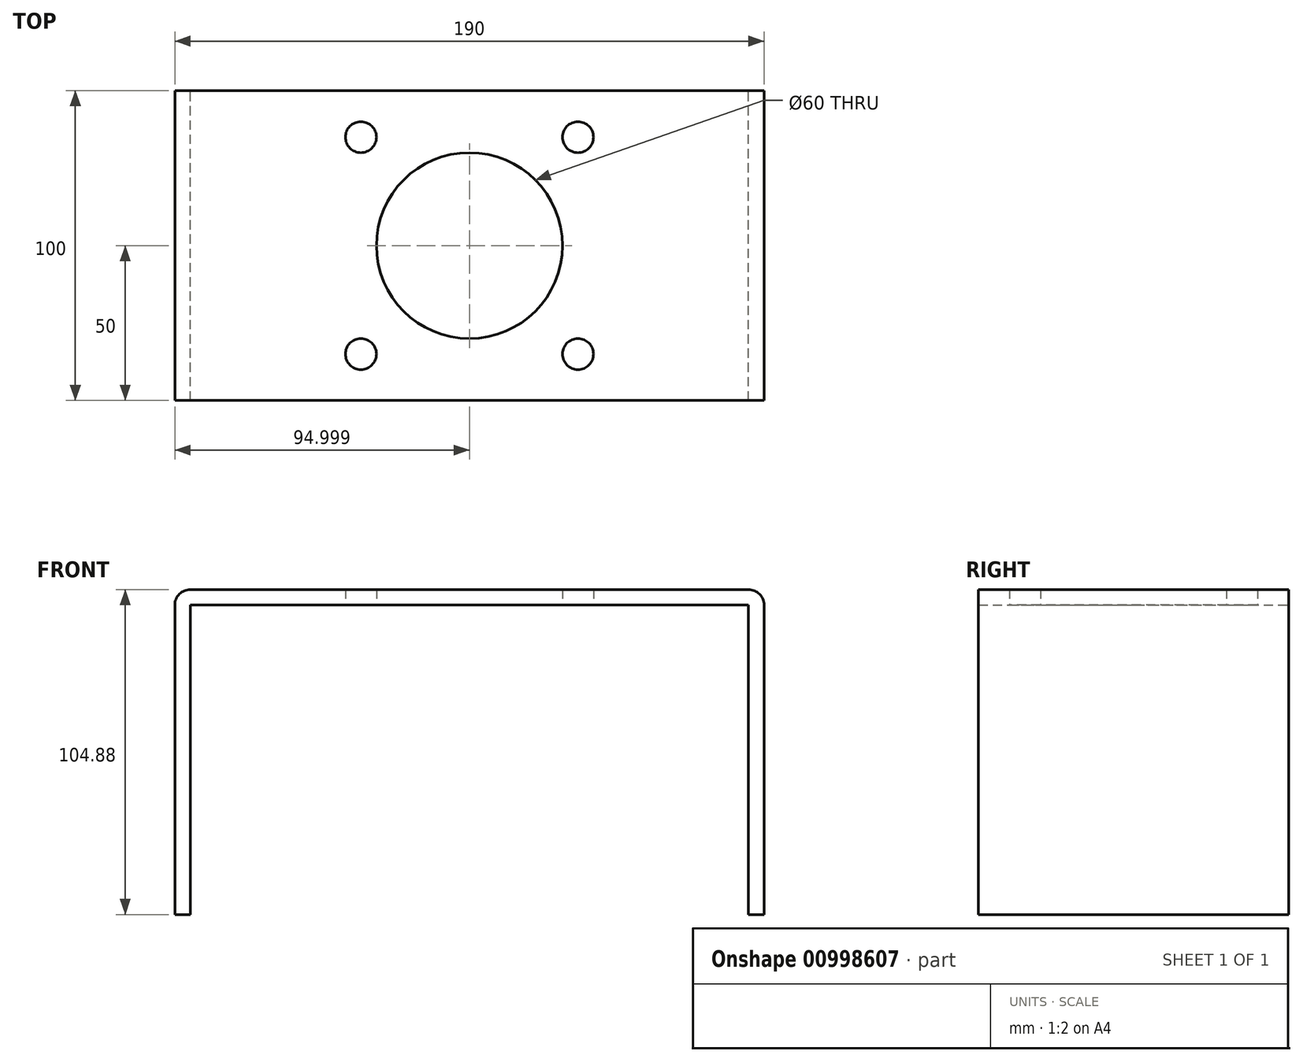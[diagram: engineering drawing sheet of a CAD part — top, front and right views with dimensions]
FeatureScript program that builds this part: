
annotation { "Feature Type Name" : "Feature", "Feature Type Description" : "" }
export const myFeature = defineFeature(function(context is Context, id is Id, definition is map)
    precondition{}
    {
        {
            var Q0;
            Q0=qCreatedBy(makeId("Front.planeOp"),FACE);
            var sketch = newSketch(context, id + "F0", { "sketchPlane" : qUnion([Q0])});
            skLineSegment(sketch, "E0", {"start": v(-104.52, 0) * mm, "end": v(-109.52, 0) * mm});
            skLineSegment(sketch, "E1", {"start": v(-109.52, 0) * mm, "end": v(-109.52, 104.88) * mm});
            skLineSegment(sketch, "E2", {"start": v(-109.52, 104.88) * mm, "end": v(80.48, 104.88) * mm});
            skLineSegment(sketch, "E3", {"start": v(80.48, 104.88) * mm, "end": v(80.48, 0) * mm});
            skLineSegment(sketch, "E4", {"start": v(80.48, 0) * mm, "end": v(75.48, 0) * mm});
            skLineSegment(sketch, "E5", {"start": v(75.48, 0) * mm, "end": v(75.48, 99.88) * mm});
            skLineSegment(sketch, "E6", {"start": v(75.48, 99.88) * mm, "end": v(-104.52, 99.88) * mm});
            skLineSegment(sketch, "E7", {"start": v(-104.52, 99.88) * mm, "end": v(-104.52, 0) * mm});
            skSolve(sketch);
        }
        {
            var Q0;
            Q0 = qSketchRegion(id + "F0", true);
            extrude(context, id + "F1", {"entities" : qUnion([Q0]), "depth" : 100 * mm, "offsetDistance" : 25 * mm});
        }
        {
            var Q0;
            Q0=makeQuery(id+"F1.opExtrude","SWEPT_EDGE",EDGE,{"disambiguationData":[OSD([sQuery(id+"F0.wireOp",EDGE,"E2"),sQuery(id+"F0.wireOp",EDGE,"E3")])]});
            var Q1;
            Q1=makeQuery(id+"F1.opExtrude","SWEPT_EDGE",EDGE,{"disambiguationData":[OSD([sQuery(id+"F0.wireOp",EDGE,"E1"),sQuery(id+"F0.wireOp",EDGE,"E2")])]});
            fillet(context, id + "F2", {"entities" : qUnion([Q0, Q1]), "radius" : 5 * mm, "tangentPropagation" : true, "allowEdgeOverflow" : false});
        }
        {
            var Q0;
            Q0=qCreatedBy(makeId("Top.planeOp"),FACE);
            var sketch = newSketch(context, id + "F3", { "sketchPlane" : qUnion([Q0])});
            skLineSegment(sketch, "E8", {"start": v(-14.52, 0) * mm, "end": v(-14.52, -98.34) * mm});
            skLineSegment(sketch, "E9", {"start": v(-104.96, -50) * mm, "end": v(75.66, -50) * mm});
            skPoint(sketch, "E10", {"position": v(-14.52, -50) * mm});
            skSolve(sketch);
        }
        {
            var Q0;
            Q0=sQuery(id+"F3.wireOp",VERTEX,"E10");
            var Q1;
            Q1=makeQuery(id+"F1.opExtrude","SWEPT_BODY",BODY,{"disambiguationData":[OSD([sQuery(id+"F0.wireOp",EDGE,"E0"),sQuery(id+"F0.wireOp",EDGE,"E1"),sQuery(id+"F0.wireOp",EDGE,"E2"),sQuery(id+"F0.wireOp",EDGE,"E3"),sQuery(id+"F0.wireOp",EDGE,"E4"),sQuery(id+"F0.wireOp",EDGE,"E5"),sQuery(id+"F0.wireOp",EDGE,"E6"),sQuery(id+"F0.wireOp",EDGE,"E7")])]});
            hole(context, id + "F4", {"style" : HoleStyle.SIMPLE, "endStyle" : HoleEndStyle.THROUGH, "oppositeDirection" : true, "holeDiameter" : 60 * mm, "majorDiameter" : 5 * mm, "isTappedThrough" : true, "tappedDepth" : 14.75 * mm, "tapClearance" : 3, "locations" : qUnion([Q0]), "scope" : qUnion([Q1])});
        }
        {
            var Q0;
            Q0=qCreatedBy(makeId("Top.planeOp"),FACE);
            var sketch = newSketch(context, id + "F5", { "sketchPlane" : qUnion([Q0])});
            skLineSegment(sketch, "E11", {"start": v(-14.52, 0) * mm, "end": v(-14.52, -100.28) * mm});
            skLineSegment(sketch, "E12", {"start": v(-104.36, -50) * mm, "end": v(74.46, -50) * mm});
            skLineSegment(sketch, "E13", {"start": v(-65.86, -15) * mm, "end": v(49.47, -15) * mm});
            skLineSegment(sketch, "E14", {"start": v(-62.73, -85) * mm, "end": v(55.34, -85) * mm});
            skLineSegment(sketch, "E15", {"start": v(-49.52, 7.44) * mm, "end": v(-49.52, -109.85) * mm});
            skLineSegment(sketch, "E16", {"start": v(20.48, 10.57) * mm, "end": v(20.48, -111.8) * mm});
            skPoint(sketch, "E17", {"position": v(-49.52, -15) * mm});
            skPoint(sketch, "E18", {"position": v(20.48, -15) * mm});
            skPoint(sketch, "E19", {"position": v(20.48, -85) * mm});
            skPoint(sketch, "E20", {"position": v(-49.52, -85) * mm});
            skSolve(sketch);
        }
        {
            var Q0;
            Q0=sQuery(id+"F5.wireOp",VERTEX,"E17");
            var Q1;
            Q1=sQuery(id+"F5.wireOp",VERTEX,"E18");
            var Q2;
            Q2=sQuery(id+"F5.wireOp",VERTEX,"E19");
            var Q3;
            Q3=sQuery(id+"F5.wireOp",VERTEX,"E20");
            var Q4;
            Q4=makeQuery(id+"F1.opExtrude","SWEPT_BODY",BODY,{"disambiguationData":[OSD([sQuery(id+"F0.wireOp",EDGE,"E0"),sQuery(id+"F0.wireOp",EDGE,"E1"),sQuery(id+"F0.wireOp",EDGE,"E2"),sQuery(id+"F0.wireOp",EDGE,"E3"),sQuery(id+"F0.wireOp",EDGE,"E4"),sQuery(id+"F0.wireOp",EDGE,"E5"),sQuery(id+"F0.wireOp",EDGE,"E6"),sQuery(id+"F0.wireOp",EDGE,"E7")])]});
            hole(context, id + "F6", {"style" : HoleStyle.SIMPLE, "endStyle" : HoleEndStyle.THROUGH, "oppositeDirection" : true, "holeDiameter" : 10 * mm, "majorDiameter" : 5 * mm, "isTappedThrough" : true, "tappedDepth" : 14.75 * mm, "tapClearance" : 3, "locations" : qUnion([Q0, Q1, Q2, Q3]), "scope" : qUnion([Q4])});
        }
    });
